# Revit family: Keilhauer-Melete-Chair-4_Leg_Steel-Arm-
name_source: partatom
category: Furniture
revit_build: Autodesk Revit 2016 (Build: 20150220_1215(x64)
units: mm (PartAtom-declared; Revit-internal decimal feet)

## family parameters
Always vertical = Yes
Cut with Voids When Loaded = No
OmniClass Number = 23.40.20.00
OmniClass Title = General Furniture and Specialties
Room Calculation Point = No
Shared = No
Work Plane-Based = No

## types (2) — shared parameters
Assembly Code = E2020200
Depth = 23 1/2"
Height = 35 1/2"
Keynote = 12500
Low Emitting Finish = Yes
Low Emitting Material = Yes
Manufacturer = Keilhauer
Product Documentation Link = https://keilhauer.com
Revit File Built By = https://servex-us.com
Salvage or Reuse = Yes
Type Comments = Melete
URL = https://keilhauer.com
Width = 21 1/2"
zero-valued in all types: Percentage of Recycled Content

## per-type parameters (varying)
| type | Description | Seat Pad |
| 83042 | Side chair with a plastic back and seat, arms and 4-leg steel base | No |
| 83052 | Side chair with a plastic back, upholstered seat, arms and 4-leg steel base | Yes |

note: column(s) folded — value = type name in every type: Model

## geometry (parser evidence)
native form markers: Sweep x5
no freeform markers — native parametric forms only
